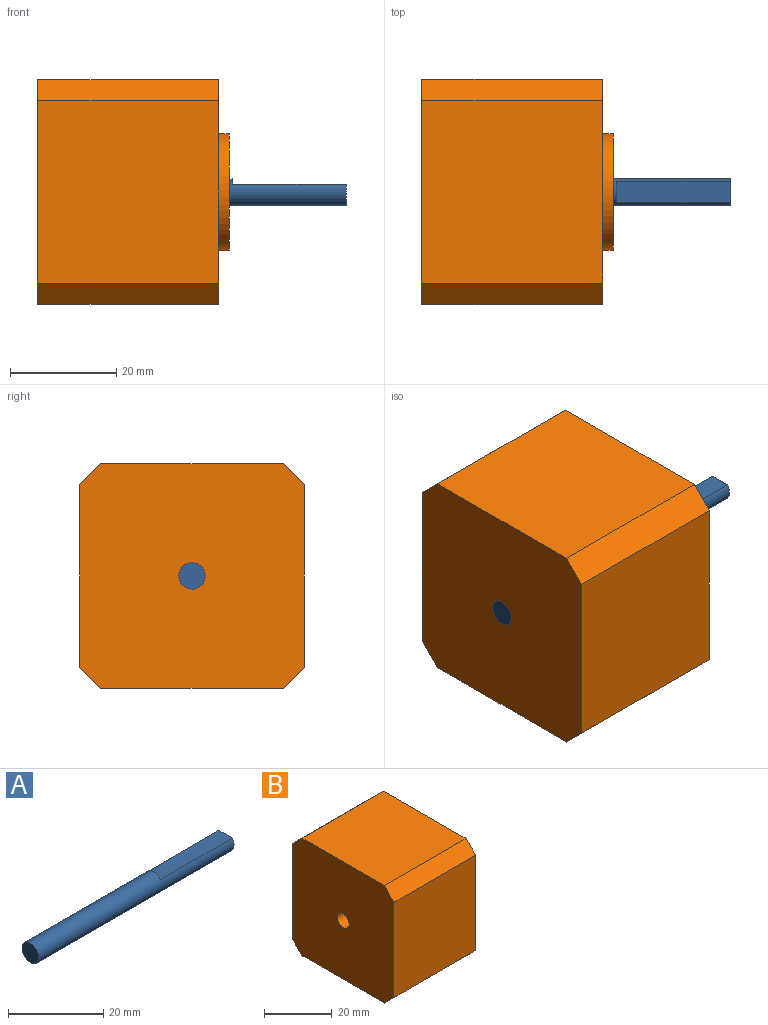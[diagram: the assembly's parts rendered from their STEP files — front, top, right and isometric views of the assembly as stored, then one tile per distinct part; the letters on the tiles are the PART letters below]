
ASSEMBLY  parts=2 mates=1
PART A: 5 faces, bbox 58x5x5 mm
  f0: plane 5x4mm, normal (1,0,0), area 16.8mm2, adj f1,f3
  f1: cylinder r=2.5mm len=58mm, axis (-1,0,0), area 812.1mm2, adj f0,f2,f3,f4
  f2: plane 5x5mm, normal (-1,0,0), area 19.6mm2, adj f1
  f3: plane 21.35x4mm, normal (0,0,1), area 85.4mm2, adj f0,f1,f4
  f4: plane 4x1mm, normal (1,0,0), area 2.8mm2, adj f1,f3
PART B: 21 faces, bbox 36x42.3x42.3 mm
  f0: plane 42.3x42.3mm, normal (1,0,0), area 1348.9mm2, adj f1,f3,f4,f5,f6,f7,f8,f9
  f1: plane 34.3x34mm, normal (0,0,1), area 1166.2mm2, adj f0,f2,f8,f9
  f2: plane 42.3x42.3mm, normal (-1,0,0), area 1737.7mm2, adj f1,f3,f4,f5,f6,f7,f8,f9
  f3: plane 34.3x34mm, normal (0,0,-1), area 1166.2mm2, adj f0,f2,f6,f7
  f4: plane 34.3x34mm, normal (0,-1,0), area 1166.2mm2, adj f0,f2,f6,f9
  f5: plane 34.3x34mm, normal (0,1,0), area 1166.2mm2, adj f0,f2,f7,f8
  f6: plane 34x4mm, normal (0,-0.71,-0.71), area 192.3mm2, adj f0,f2,f3,f4
  f7: plane 34x4mm, normal (0,0.71,-0.71), area 192.3mm2, adj f0,f2,f3,f5
  f8: plane 34x4mm, normal (0,0.71,0.71), area 192.3mm2, adj f0,f1,f2,f5
  f9: plane 34x4mm, normal (0,-0.71,0.71), area 192.3mm2, adj f0,f1,f2,f4
  f10: cylinder r=11mm len=22mm, axis (-1,0,0), area 138.2mm2, adj f0,f11
  f11: plane 22x22mm, normal (1,0,0), area 360.5mm2, adj f10,f20
  f12: cylinder r=1.5mm len=4.5mm, axis (1,0,0), area 42.4mm2, adj f0,f13
  f13: plane 3x3mm, normal (1,0,0), area 7.1mm2, adj f12
  f14: cylinder r=1.5mm len=4.5mm, axis (1,0,0), area 42.4mm2, adj f0,f15
  f15: plane 3x3mm, normal (1,0,0), area 7.1mm2, adj f14
  f16: cylinder r=1.5mm len=4.5mm, axis (1,0,0), area 42.4mm2, adj f0,f17
  f17: plane 3x3mm, normal (1,0,0), area 7.1mm2, adj f16
  f18: cylinder r=1.5mm len=4.5mm, axis (1,0,0), area 42.4mm2, adj f0,f19
  f19: plane 3x3mm, normal (1,0,0), area 7.1mm2, adj f18
  f20: cylinder r=2.5mm len=36mm, axis (-1,0,0), area 565.5mm2, adj f2,f11
PLACE A t=(77.77,0,14.42)mm
PLACE B t=(77.77,0,14.42)mm fixed
MATE revolute B.f20 <-> A.f1  axis (-1,0,0) through (-4.23,0,14.42)mm
